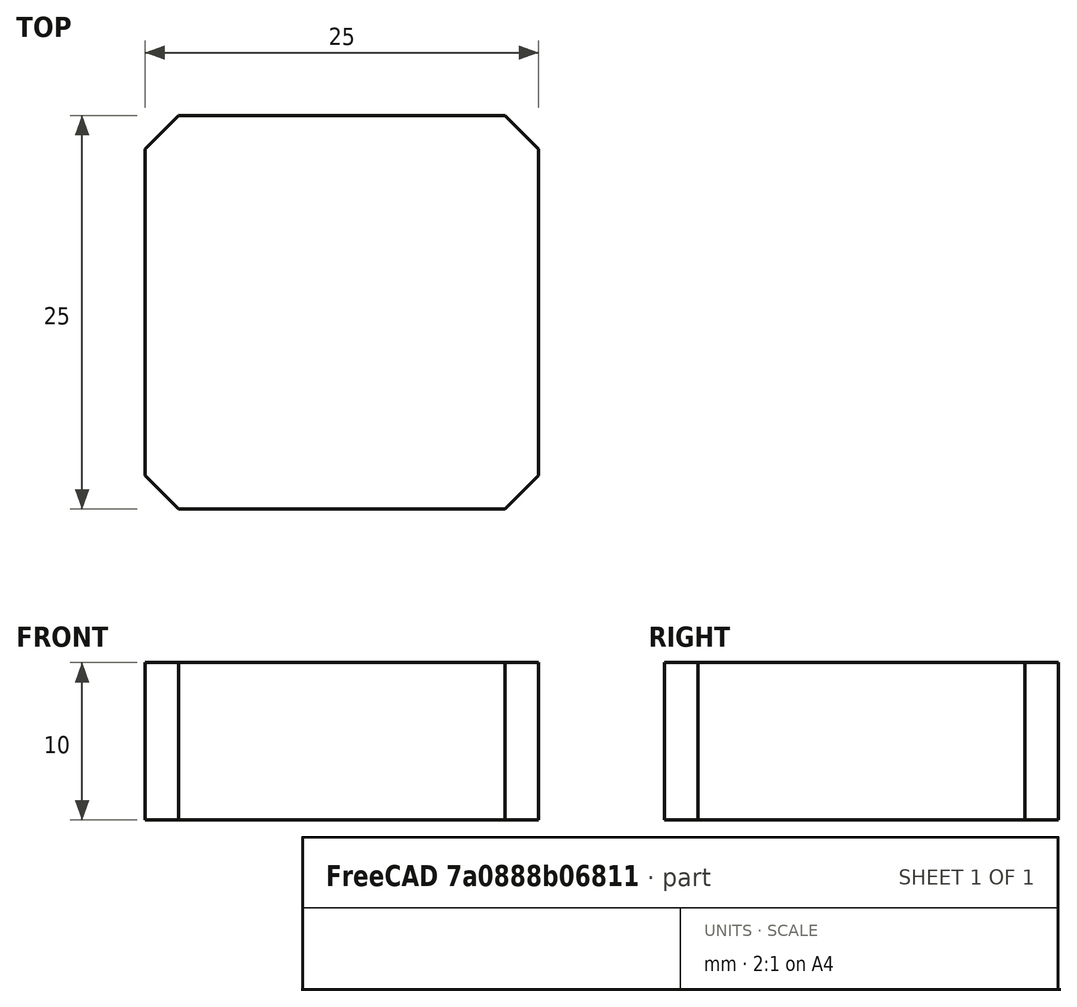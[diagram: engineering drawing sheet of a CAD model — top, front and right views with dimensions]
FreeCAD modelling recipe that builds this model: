
FCSTD DOCUMENT  (FreeCAD 1.0R39109 (Git))
Label: HiLetGo_GPS_Antenna
License: All rights reserved
LicenseURL: https://en.wikipedia.org/wiki/All_rights_reserved
objects: Sketcher::SketchObject×1, PartDesign::Pad×1, PartDesign::Body×1
note: 6 computed .brp shape members not serialized (recipe doc carries the construction recipe); baked Part::Feature solids carry a one-line shape summary decoded from their .brp

FEATURE [Sketcher::SketchObject] Sketch
  ArcFitTolerance = 1e-06
  AttachmentSupport = -> [XY_Plane]
  FullyConstrained = true
  MakeInternals = false
  MapMode = 5
  sketch-geometry (16):
    g0: LineSegment StartX=-12.5 StartY=10.3787 StartZ=0 EndX=-12.5 EndY=-10.3787 EndZ=0
    g1: LineSegment StartX=-10.3787 StartY=-12.5 StartZ=0 EndX=10.3787 EndY=-12.5 EndZ=0
    g2: LineSegment StartX=12.5 StartY=-10.3787 StartZ=0 EndX=12.5 EndY=10.3787 EndZ=0
    g3: LineSegment StartX=10.3787 StartY=12.5 StartZ=0 EndX=-10.3787 EndY=12.5 EndZ=0
    g4: ArcOfCircle [constr] CenterX=10.3787 CenterY=10.3787 CenterZ=0 NormalX=0 NormalY=0 NormalZ=1 AngleXU=0 Radius=2.12132 StartAngle=0 EndAngle=1.5708
    g5: GeomPoint [constr] X=12.5 Y=12.5 Z=0
    g6: LineSegment StartX=12.5 StartY=10.3787 StartZ=0 EndX=10.3787 EndY=12.5 EndZ=0
    g7: ArcOfCircle [constr] CenterX=10.3787 CenterY=-10.3787 CenterZ=0 NormalX=0 NormalY=0 NormalZ=1 AngleXU=0 Radius=2.12132 StartAngle=4.71239 EndAngle=6.28319
    g8: GeomPoint [constr] X=12.5 Y=-12.5 Z=0
    g9: LineSegment StartX=10.3787 StartY=-12.5 StartZ=0 EndX=12.5 EndY=-10.3787 EndZ=0
    g10: ArcOfCircle [constr] CenterX=-10.3787 CenterY=-10.3787 CenterZ=0 NormalX=0 NormalY=0 NormalZ=1 AngleXU=0 Radius=2.12132 StartAngle=3.14159 EndAngle=4.71239
    g11: GeomPoint [constr] X=-12.5 Y=-12.5 Z=0
    g12: LineSegment StartX=-12.5 StartY=-10.3787 StartZ=0 EndX=-10.3787 EndY=-12.5 EndZ=0
    g13: ArcOfCircle [constr] CenterX=-10.3787 CenterY=10.3787 CenterZ=0 NormalX=0 NormalY=0 NormalZ=1 AngleXU=0 Radius=2.12132 StartAngle=1.5708 EndAngle=3.14159
    g14: GeomPoint [constr] X=-12.5 Y=12.5 Z=0
    g15: LineSegment StartX=-10.3787 StartY=12.5 StartZ=0 EndX=-12.5 EndY=10.3787 EndZ=0
  constraints (35):
    c: Vertical(g0)
    c: Vertical(g2)
    c: Horizontal(g1)
    c: Horizontal(g3)
    c: Symmetric(g14,g8,g-1)
    c: Distance(g5,g14) = 25
    c: PointOnObject(g5,g3)
    c: PointOnObject(g5,g2)
    c: Tangent(g3,g4) = -1.5708
    c: Tangent(g2,g4) = -1.5708
    c: Coincident(g6,g3)
    c: Coincident(g6,g2)
    c: PointOnObject(g8,g2)
    c: PointOnObject(g8,g1)
    c: Tangent(g2,g7) = -1.5708
    c: Tangent(g1,g7) = -1.5708
    c: Coincident(g9,g2)
    c: Coincident(g9,g1)
    c: PointOnObject(g11,g0)
    c: PointOnObject(g11,g1)
    c: Tangent(g0,g10) = -1.5708
    c: Tangent(g1,g10) = -1.5708
    c: Coincident(g12,g0)
    c: Coincident(g12,g1)
    c: PointOnObject(g14,g0)
    c: PointOnObject(g14,g3)
    c: Tangent(g0,g13) = -1.5708
    c: Tangent(g3,g13) = -1.5708
    c: Coincident(g15,g0)
    c: Coincident(g15,g3)
    c: Distance(g1,g3) = 25
    c: Equal(g15,g6)
    c: Equal(g6,g9)
    c: Equal(g9,g12)
    c: Distance(g15,g15) = 3
FEATURE [PartDesign::Pad] Pad
  Direction = (0,0,1)
  Length = 10
  Length2 = 10
  Profile = -> Sketch
  ReferenceAxis = -> Sketch [N_Axis]
  Refine = true
  Suppressed = false
  Type = 0
FEATURE [PartDesign::Body] Body  label="HiLetGo_GPS_Antenna"
  AllowCompound = false
  Group = -> [Sketch,Pad]
  Origin = -> Origin
  Tip = -> Pad
